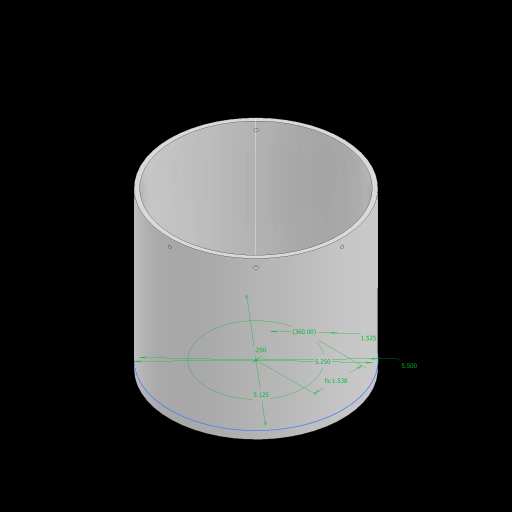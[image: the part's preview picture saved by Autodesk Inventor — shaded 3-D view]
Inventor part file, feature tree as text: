
AUTODESK INVENTOR PART (.ipt)
format: ipt  version: 2023 (Build 270158000, 158)  size: 163,328 bytes
history: native  units: in
note: dims shown in document units (in); Inventor stores cm internally (conversion verified against a paired STEP export)
features: extrude x5, sketch x3, pattern_circular x3, plane x1
ambient origin geometry x8: Origin, YZ Plane, XZ Plane, XY Plane, X Axis, Y Axis, Z Axis, Center Point
bodies: Solid1 (feature_tree)
feature tree (12):
  sketch  "Sketch1"  dims[d0=5.25in]
  extrude  "Extrusion1"  Depth=0.25in
  extrude  "Extrusion2"  Depth=0.25in TaperAngle=0.0deg
  plane  "Work Plane1"
  sketch  "Sketch2"  dims[d2=1.5748in d3=5.125in d4=1.525in d5=1.5375in d6=360.0deg d7=0.25in d8=5.5in]
  extrude  "Extrusion3"  Depth=0.25in
  pattern_circular  "Circular Pattern1"  [2 undecoded]
  extrude  "Extrusion4"  Depth=0.25in
  pattern_circular  "Circular Pattern2"  [2 undecoded]
  extrude  "Extrusion5"  Depth=0.25in TaperAngle=360.0deg
  pattern_circular  "Circular Pattern3"  [2 undecoded]
  sketch  "Sketch3"  dims[d9=4.75in d10=0.0in d11=0.25in d12=0.0in d13=2.75in d14=0.1in d15=0.25in d16=0.1in d17=0.0in d18=3.1496in d19=360.0deg d21=1.0in d22=0.0in d23=1.5748in d24=360.0deg d26=0.1in d27=1.5in d28=4.75in d29=0.0in d30=1.5748in d31=360.0deg]
note: 6 required parameter values undecoded (feature->parameter linkage not recoverable at this tier; creation-order binding heuristic only, values carry confidence <= 0.55)
